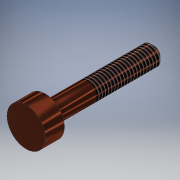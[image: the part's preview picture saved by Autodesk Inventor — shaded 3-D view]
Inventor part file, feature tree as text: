
AUTODESK INVENTOR PART (.ipt)
format: ipt  version: 2017 (Build 210142000, 142)  size: 116,736 bytes
history: native  units: mm
features: extrude x2, sketch x2, thread x1, chamfer x1
ambient origin geometry x8: Origin, YZ Plane, XZ Plane, XY Plane, X Axis, Y Axis, Z Axis, Center Point
bodies: Solid1 (feature_tree)
feature tree (6):
  extrude  "Extrusion1"  Depth=3.0mm TaperAngle=0.0deg
  extrude  "Extrusion2"  Depth=17.0mm TaperAngle=0.0deg
  thread  "Thread1"  [1 undecoded]
  chamfer  "Chamfer1"  Distance=0.5mm Angle=45.0deg
  sketch  "Sketch1"  dims[d0=6.0mm d1=3.0mm d2=0.0mm]
  sketch  "Sketch2"  dims[d3=3.0mm d4=17.0mm d5=0.0mm d6=10.0mm d7=0.5mm d8=0.5mm d9=2.0mm d10=45.0deg]
note: 1 required parameter value undecoded (feature->parameter linkage not recoverable at this tier; creation-order binding heuristic only, values carry confidence <= 0.55)
